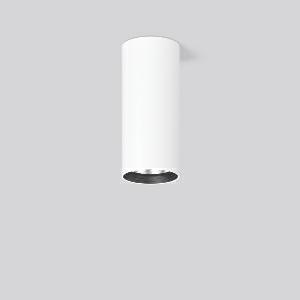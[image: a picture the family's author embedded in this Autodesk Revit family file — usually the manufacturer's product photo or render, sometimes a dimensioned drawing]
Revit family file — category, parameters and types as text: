
# Revit family: heledon_mini_a_931202_002_76_6c0a
name_source: partatom
category: Lighting Fixtures
units: mm (PartAtom-declared; Revit-internal decimal feet)

## family parameters
Cut with Voids When Loaded = No
Host = Face
Light Source = No
Part Type = Normal
Room Calculation Point = No
Round Connector Dimension = Use Diameter
Shared = No

## types (1)
- HELEDON mini A (1 x LED Modul 930, 2550 lm, 3000)
    Apparent Load = 20 VA
    Approval mark = CE
    CIE Flux Codes = 95 99 100 100 100
    Color Rendering = 90
    Color Temperature = 3000
    Default Elevation = 1800 mm
    Description = Series: HELEDON mini
Cylindrical surface-mounted downlight. Housing: die-cast aluminium, powder-coated. Internal ceiling frame polycarbonate with bayonet mounting. Black plastic ring and recessed LED to prevent glare from the side. Optical assembly with reflector made of MIRO-Silver with 98% total light reflection for outstanding efficiency - can be changed without tools. Best colour rendering index Ra>90. Suitable for Ceiling mounting. Easy installation with a separate ceiling frame with bayonet mounting and plug connection. Driver integrated. Connected via plug-in connector. High quality converter without flickering and stroboscopic effect. The following accessories can be mounted without use of tools: interchangeable lenses, decorative glasses, honeycomb louvre, clear and frosted diffusers, white interchangeable plastic ring. 
Colour: traffic white, matt (RAL 9016)
Diameter: 87 mm
Height: 197 mm
Lamp: LED
Socket: without socket
Colour temperature: 3000K
Colour rendering index (CRI): 92
System power: 20 W
Rated luminous flux: 2550 lm
Luminous efficiency: 128 lm/W
Control gear: Converter, dimmable, DALI
Protection class: I
Type of protection: IP 20
    Height = 197 mm
    Lamp = 1 x LED Modul 930
    Lamp Light Flux = 2550 lm
    Lamp count = 1
    Length = 87 mm
    Lifetime = 50000 h
    Luminous efficacy = 128 lm/W
    Manufacturer = RZB
    ModVariant = No
    Model = 931202.002.76
    Mounting Place = Ceiling
    Mounting Type = Surface mounted
    Number of Poles = 1
    OnlyDefault = Yes
    Power Factor = 1
    Product Name = HELEDON mini A
    Product group = Surface mounted downlights
    ProductGroupID = 302
    Protection Class = Protection class I
    Protection Degree = IP 20
    RLX_Detail_Level = 1
    RLX_Emergency_Light_Flux = 0 lm
    RLX_Emergency_Type = 0
    RLX_Emergency_Type_DB = No
    RlxData = <blob elided: 104961 chars, md5=c3d9c6eb>
    Socket = socket
    Standby Power = 0 W
    System Light Flux = 2550 lm
    System Power = 20 W
    Type Comments = Product without accessories
    Type Image = 931188.002.jpg
    URL = http://relux.com
    VarID = ---
    Voltage = 230 V
    Voltage Range = 220-240 V
    Weight = 0.00 kg
    Width = 0 mm  [stored 0 ft]

note: [stored X ft] marks values corroborated as IEEE doubles in the binary element streams (Revit-internal decimal feet)

## geometry (parser evidence)
native form markers: Blend x4, Sweep x10
no freeform markers — native parametric forms only
